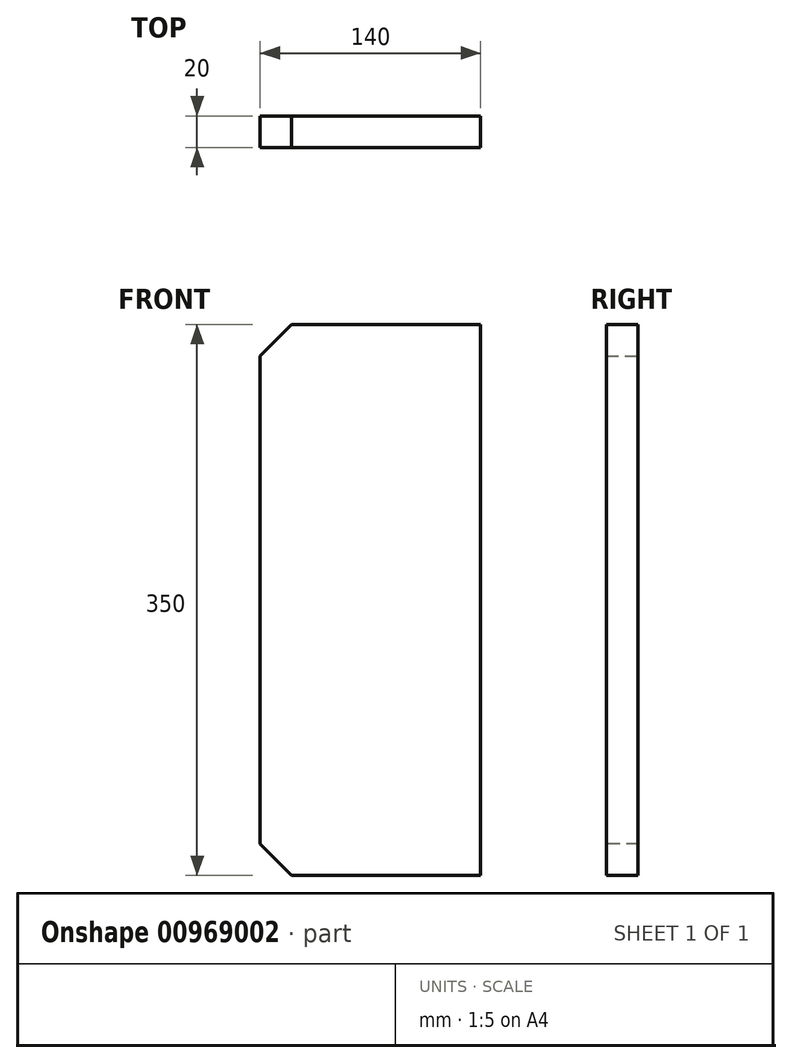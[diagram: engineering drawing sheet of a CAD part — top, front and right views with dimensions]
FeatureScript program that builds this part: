
annotation { "Feature Type Name" : "Feature", "Feature Type Description" : "" }
export const myFeature = defineFeature(function(context is Context, id is Id, definition is map)
    precondition{}
    {
        {
            var Q0;
            Q0=qCreatedBy(makeId("Front.planeOp"),FACE);
            var sketch = newSketch(context, id + "F0", { "sketchPlane" : qUnion([Q0])});
            skLineSegment(sketch, "E0.bottom", {"start": v(70, 175) * mm, "end": v(-70, 175) * mm});
            skLineSegment(sketch, "E0.top", {"start": v(70, -175) * mm, "end": v(-70, -175) * mm});
            skLineSegment(sketch, "E0.left", {"start": v(70, 175) * mm, "end": v(70, -175) * mm});
            skLineSegment(sketch, "E0.right", {"start": v(-70, 175) * mm, "end": v(-70, -175) * mm});
            skPoint(sketch, "E0.middle", {"position": v(0, 0) * mm});
            skSolve(sketch);
        }
        {
            var Q0;
            Q0=makeQuery(id+"F0.imprint","IMPRINT",FACE,{"disambiguationData":[TD([[makeQuery(id+"F0.imprint","IMPRINT",EDGE,{"derivedFrom":sQuery(id+"F0.wireOp",EDGE,"E0.bottom")}),1.0]])]});
            extrude(context, id + "F1", {"entities" : qUnion([Q0]), "depth" : 20 * mm, "offsetDistance" : 25 * mm});
        }
        {
            var Q0;
            Q0=makeQuery(id+"F1.opExtrude","SWEPT_EDGE",EDGE,{"disambiguationData":[OSD([sQuery(id+"F0.wireOp",EDGE,"E0.bottom"),sQuery(id+"F0.wireOp",EDGE,"E0.right")])]});
            var Q1;
            Q1=makeQuery(id+"F1.opExtrude","SWEPT_EDGE",EDGE,{"disambiguationData":[OSD([sQuery(id+"F0.wireOp",EDGE,"E0.top"),sQuery(id+"F0.wireOp",EDGE,"E0.right")])]});
            chamfer(context, id + "F2", {"entities" : qUnion([Q0, Q1]), "width" : 20 * mm, "tangentPropagation" : true});
        }
    });
